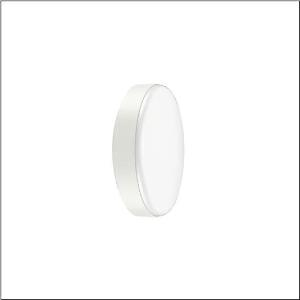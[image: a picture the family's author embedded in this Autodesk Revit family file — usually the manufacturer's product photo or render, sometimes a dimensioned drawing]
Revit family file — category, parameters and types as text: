
# Revit family: round_31_51wc10da42as
name_source: partatom
category: Lighting Fixtures
units: mm (PartAtom-declared; Revit-internal decimal feet)

## family parameters
Cut with Voids When Loaded = No
Host = Face
Light Source = No
Part Type = Normal
Room Calculation Point = No
Round Connector Dimension = Use Diameter
Shared = No

## types (1)
- Round 31 (1 x LED, 2550 lm, 20.5 W, 4000K)
    Apparent Load = 21 VA
    CIE Flux Codes = 44 75 94 94 100
    Color Rendering = 80
    Color Temperature = 4000K
    Default Elevation = 1800 mm
    Description = Round 31, wall and ceiling luminaire, primary optical cover: cover, of PC, opal, light emission: direct distribution, primary light characteristic: symmetric, installation type: surface-mounted, LED, rated luminous flux: 2.550lm, luminous efficacy: 124lm/W, light colour: 840, colour temperature: 4000K, control gear: DALI 2, with terminal, 5-pole, max. 2.5mm², mains connection: 220..240V, AC, 50/60Hz, rated input power: 20.5W, luminaire housing, of PC, traffic white (RAL 9016), diameter: 350mm, brightness and presence sensor, HF sensor, protection rating (complete): IP65, insulation class (complete): insulation class II (safety insulation), certification: CE, impact resistance: IK10, permissible operating ambient temperature: -20..+40°C, permissible storage temperature: -20..+60°C, packaging unit: 1 piece
    Height = 97 mm
    Lamp = 1 x LED
    Lamp Light Flux = 2550 lm
    Lamp Power = 20.5 W
    Lamp count = 1
    Length = 350 mm
    Luminous efficacy = 124 lm/W
    Manufacturer = Siteco
    ModVariant = No
    Model = 51WC10DA42AS
    Mounting Place = Wall
    Mounting Type = Surface mounted
    Number of Poles = 1
    OnlyDefault = Yes
    Power Factor = 1
    Product Name = Round 31
    Product group = wall and ceiling luminaire
    ProductGroupID = 2001
    Protection Class = Protection class II
    Protection Degree = IP 65
    RLX_Detail_Level = 1
    RLX_Emergency_Light_Flux = 0 lm
    RLX_Emergency_Type = 0
    RLX_Emergency_Type_DB = No
    RlxData = <blob elided: 29645 chars, md5=5e03c4ec>
    Socket = socket
    Standby Power = 0 W
    System Light Flux = 2550 lm
    System Power = 21 W
    Type Comments = Product without accessories
    Type Image = l_1007027.jpg
    URL = http://relux.com
    VarID = ---
    Voltage = 0 V
    Weight = 0.00 kg
    Width = 0 mm  [stored 0 ft]

note: [stored X ft] marks values corroborated as IEEE doubles in the binary element streams (Revit-internal decimal feet)

## geometry (parser evidence)
native form markers: Blend x4, Sweep x12
no freeform markers — native parametric forms only
